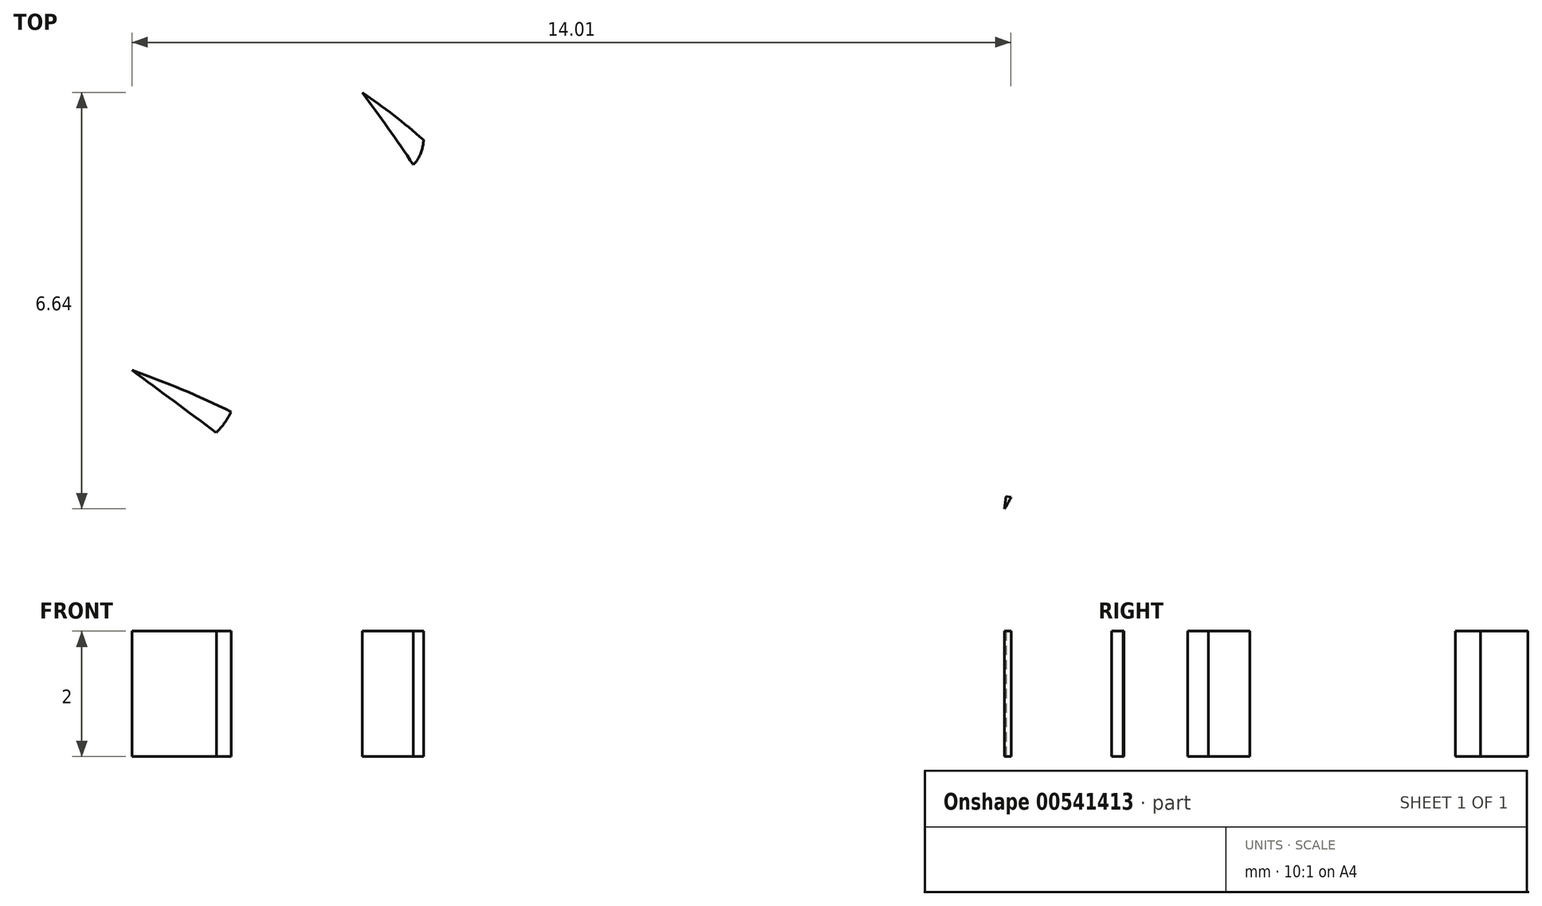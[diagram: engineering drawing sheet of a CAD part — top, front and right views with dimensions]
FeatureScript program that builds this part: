
annotation { "Feature Type Name" : "Feature", "Feature Type Description" : "" }
export const myFeature = defineFeature(function(context is Context, id is Id, definition is map)
    precondition{}
    {
        {
            var Q0;
            Q0=qCreatedBy(makeId("Top.planeOp"),FACE);
            var sketch = newSketch(context, id + "F0", { "sketchPlane" : qUnion([Q0])});
            skFitSpline(sketch, "E0", {"points": [v(-7.28, 23.86) * mm, v(-2.86, 13.8) * mm, v(-10.95, 19.43) * mm], "startDerivative": vector(18.39, -24.25) * mm, "endDerivative": vector(-31.57, 11.1) * mm});
            skFitSpline(sketch, "E1", {"points": [v(-7.28, 23.86) * mm, v(-3.4, 19.4) * mm, v(-2.4, 24.55) * mm], "startDerivative": vector(15.72, -10.48) * mm, "endDerivative": vector(5.56, 16.47) * mm});
            skFitSpline(sketch, "E2", {"points": [v(-2.4, 24.55) * mm, v(-1.89, 15.31) * mm, v(-0.1, 9.05) * mm], "startDerivative": vector(-4.2, -34.55) * mm, "endDerivative": vector(9.1, -27.73) * mm});
            skFitSpline(sketch, "E3", {"points": [v(2.74, 21.8) * mm, v(2.33, 14.08) * mm, v(-0.1, 9.05) * mm], "startDerivative": vector(3.5, -17.09) * mm, "endDerivative": vector(-8.14, -6.33) * mm});
            skFitSpline(sketch, "E4", {"points": [v(2.74, 21.8) * mm, v(3.37, 15.56) * mm, v(2.5, 12.07) * mm], "startDerivative": vector(6.44, -9.2) * mm, "endDerivative": vector(-5.09, -24.27) * mm});
            skFitSpline(sketch, "E5", {"points": [v(2.5, 12.07) * mm, v(5.64, 13.91) * mm, v(9.18, 17.17) * mm], "startDerivative": vector(11.84, 4.8) * mm, "endDerivative": vector(6.3, 8.36) * mm});
            skFitSpline(sketch, "E6", {"points": [v(9.18, 17.17) * mm, v(6.35, 13.6) * mm, v(2.5, 10.84) * mm], "startDerivative": vector(-3.85, -9.64) * mm, "endDerivative": vector(-10.17, -6.25) * mm});
            skFitSpline(sketch, "E7", {"points": [v(-2, 11.23) * mm, v(-1.24, 6.46) * mm, v(-1.28, 2.27) * mm], "startDerivative": vector(2.67, -9.53) * mm, "endDerivative": vector(-2.9, -13.25) * mm});
            skFitSpline(sketch, "E8", {"points": [v(2.5, 10.84) * mm, v(0.47, 6.67) * mm, v(1.91, -4.86) * mm], "startDerivative": vector(-6.92, -10.08) * mm, "endDerivative": vector(0, 3.84) * mm});
            skFitSpline(sketch, "E9", {"points": [v(-10.1, 11.97) * mm, v(-6.04, 6.59) * mm, v(-1.28, 2.27) * mm], "startDerivative": vector(-0.34, -15.68) * mm, "endDerivative": vector(0, 6.82) * mm});
            skFitSpline(sketch, "E10", {"points": [v(10.4, 11.36) * mm, v(7.8, 1.76) * mm, v(1.91, -4.86) * mm], "startDerivative": vector(-2.43, -20.8) * mm, "endDerivative": vector(-4.14, 2.7) * mm});
            skFitSpline(sketch, "E11", {"points": [v(10.4, 11.36) * mm, v(9.84, 4.76) * mm, v(7.52, -0.1) * mm], "startDerivative": vector(5.3, -7.8) * mm, "endDerivative": vector(-5.92, -9.7) * mm});
            skFitSpline(sketch, "E12", {"points": [v(7.52, -0.1) * mm, v(13.28, 2.8) * mm, v(21.16, 4.47) * mm], "startDerivative": vector(11.55, 6.87) * mm, "endDerivative": vector(21.33, -3.14) * mm});
            skFitSpline(sketch, "E13", {"points": [v(-10.1, 11.97) * mm, v(-9.26, 8.16) * mm, v(-16.19, 10.72) * mm], "startDerivative": vector(-8.08, -15.34) * mm, "endDerivative": vector(-18.86, 4.84) * mm});
            skFitSpline(sketch, "E14", {"points": [v(-16.19, 10.72) * mm, v(-6.94, 6.04) * mm, v(-16.19, 5.22) * mm], "startDerivative": vector(40.48, -21.8) * mm, "endDerivative": vector(-62.27, 1.8) * mm});
            skFitSpline(sketch, "E15", {"points": [v(-1.35, -0.04) * mm, v(-1.42, -8.86) * mm, v(-20.96, 0.93) * mm], "startDerivative": vector(7.31, -30.06) * mm, "endDerivative": vector(-51.62, -16.27) * mm});
            skFitSpline(sketch, "E16", {"points": [v(11.85, 1.07) * mm, v(2.54, -18.35) * mm, v(5.68, -37.82) * mm], "startDerivative": vector(-64.96, -24.6) * mm, "endDerivative": vector(16.53, -39.43) * mm});
            skFitSpline(sketch, "E17", {"points": [v(11.85, 1.07) * mm, v(19.18, 1.07) * mm, v(12.97, 1.76) * mm], "startDerivative": vector(22.33, -1.93) * mm, "endDerivative": vector(-7.46, -0.54) * mm});
            skFitSpline(sketch, "E18", {"points": [v(12.97, 1.76) * mm, v(16.44, 3.4) * mm, v(21.16, 4.47) * mm], "startDerivative": vector(7, 3.83) * mm, "endDerivative": vector(9.33, 1.62) * mm});
            skFitSpline(sketch, "E19", {"points": [v(-20.96, 0.93) * mm, v(-6.66, -5.68) * mm, v(-18.96, -5.83) * mm], "startDerivative": vector(45.61, 4.03) * mm, "endDerivative": vector(-48.6, -15.15) * mm});
            skFitSpline(sketch, "E20", {"points": [v(-18.96, -5.83) * mm, v(-1.16, -18.25) * mm, v(-8.26, -37.47) * mm], "startDerivative": vector(95.98, 3.77) * mm, "endDerivative": vector(-30.97, -39) * mm});
            skLineSegment(sketch, "E21", {"start": v(-8.26, -37.47) * mm, "end": v(5.68, -37.82) * mm});
            skFitSpline(sketch, "E22", {"points": [v(-13.45, 22.99) * mm, v(-14.02, 22.6) * mm, v(-13.4, 21.65) * mm], "startDerivative": vector(1.91, -4.42) * mm, "endDerivative": vector(-3.84, -0.79) * mm});
            skFitSpline(sketch, "E23", {"points": [v(-13.4, 21.65) * mm, v(-12.9, 20.9) * mm, v(-12.95, 20.25) * mm], "startDerivative": vector(-4.2, -3.2) * mm, "endDerivative": vector(-4.26, -2.28) * mm});
            skFitSpline(sketch, "E24", {"points": [v(-12.95, 20.25) * mm, v(-11.98, 19.71) * mm, v(-11.6, 19.12) * mm], "startDerivative": vector(-2.53, -3.4) * mm, "endDerivative": vector(-2.97, -4.02) * mm});
            skFitSpline(sketch, "E25", {"points": [v(-11.6, 19.12) * mm, v(-10.75, 18.89) * mm, v(-10.27, 18.52) * mm], "startDerivative": vector(-0.2, -3.23) * mm, "endDerivative": vector(1.3, -3.45) * mm});
            skFitSpline(sketch, "E26", {"points": [v(-10.27, 18.52) * mm, v(-9.31, 18.95) * mm, v(-9.34, 19.63) * mm], "startDerivative": vector(1.56, -3.6) * mm, "endDerivative": vector(1.97, 2.6) * mm});
            skFitSpline(sketch, "E27", {"points": [v(-9.34, 19.63) * mm, v(-9.7, 19.93) * mm, v(-9.46, 20.67) * mm], "startDerivative": vector(1.95, 4.8) * mm, "endDerivative": vector(2.77, 2.16) * mm});
            skFitSpline(sketch, "E28", {"points": [v(-9.46, 20.67) * mm, v(-9.73, 21.28) * mm, v(-10.33, 22.47) * mm], "startDerivative": vector(1.33, 6.6) * mm, "endDerivative": vector(1.65, 8.03) * mm});
            skFitSpline(sketch, "E29", {"points": [v(-10.33, 22.47) * mm, v(-10.9, 22.62) * mm, v(-11.47, 23.44) * mm], "startDerivative": vector(-1.13, 5.1) * mm, "endDerivative": vector(-0.22, 4.49) * mm});
            skFitSpline(sketch, "E30", {"points": [v(-11.47, 23.44) * mm, v(-12.2, 23.5) * mm, v(-12.48, 23.71) * mm], "startDerivative": vector(-1.3, 4.81) * mm, "endDerivative": vector(-1.53, 3.53) * mm});
            skFitSpline(sketch, "E31", {"points": [v(-12.48, 23.71) * mm, v(-13.17, 23.6) * mm, v(-13.45, 22.99) * mm], "startDerivative": vector(-1.7, -4.44) * mm, "endDerivative": vector(2.22, -3.82) * mm});
            skFitSpline(sketch, "E32", {"points": [v(-1.35, 21.75) * mm, v(-1.42, 21.15) * mm, v(-1.8, 20.76) * mm], "startDerivative": vector(-0.58, -0.6) * mm, "endDerivative": vector(1.68, -4.51) * mm});
            skFitSpline(sketch, "E33", {"points": [v(-1.8, 20.76) * mm, v(-2.11, 20.22) * mm, v(-1.78, 19.23) * mm], "startDerivative": vector(2.85, -4.12) * mm, "endDerivative": vector(3.48, -0.95) * mm});
            skFitSpline(sketch, "E34", {"points": [v(-1.78, 19.23) * mm, v(-1.62, 18.4) * mm, v(-1.1, 17.14) * mm], "startDerivative": vector(5.03, -3.08) * mm, "endDerivative": vector(9.15, -4.78) * mm});
            skFitSpline(sketch, "E35", {"points": [v(-1.1, 17.14) * mm, v(-0.27, 16.66) * mm, v(0.64, 15.82) * mm], "startDerivative": vector(7.65, 0.86) * mm, "endDerivative": vector(9.97, 1.24) * mm});
            skFitSpline(sketch, "E36", {"points": [v(0.64, 15.82) * mm, v(1.16, 15.52) * mm, v(2.74, 14.9) * mm], "startDerivative": vector(7.16, 2.4) * mm, "endDerivative": vector(7.15, 0.46) * mm});
            skFitSpline(sketch, "E37", {"points": [v(2.74, 14.9) * mm, v(2.92, 15.97) * mm, v(3.06, 17.4) * mm], "startDerivative": vector(3.53, 0.84) * mm, "endDerivative": vector(3.33, 5.77) * mm});
            skFitSpline(sketch, "E38", {"points": [v(3.06, 17.4) * mm, v(2.13, 17.82) * mm, v(2.59, 19.14) * mm], "startDerivative": vector(-4.3, 0.6) * mm, "endDerivative": vector(0.65, 3.2) * mm});
            skFitSpline(sketch, "E39", {"points": [v(2.59, 19.14) * mm, v(2, 19.76) * mm, v(1.42, 21.07) * mm], "startDerivative": vector(1.7, 10.1) * mm, "endDerivative": vector(0.5, 6.87) * mm});
            skFitSpline(sketch, "E40", {"points": [v(1.42, 21.07) * mm, v(0.65, 21) * mm, v(0.13, 21.39) * mm], "startDerivative": vector(-1.39, 4.09) * mm, "endDerivative": vector(-0.65, 3.22) * mm});
            skFitSpline(sketch, "E41", {"points": [v(0.13, 21.39) * mm, v(-0.36, 21.67) * mm, v(-1.35, 21.75) * mm], "startDerivative": vector(0.09, 6.17) * mm, "endDerivative": vector(1.27, -4.42) * mm});
            skFitSpline(sketch, "E42", {"points": [v(-7.74, 24.94) * mm, v(-7.9, 24.36) * mm, v(-7.99, 24.08) * mm], "startDerivative": vector(-3.6, -2.32) * mm, "endDerivative": vector(-2.86, -0.7) * mm});
            skFitSpline(sketch, "E43", {"points": [v(-7.74, 24.94) * mm, v(-7.15, 25.05) * mm, v(-6.77, 24.94) * mm], "startDerivative": vector(0.18, 4.05) * mm, "endDerivative": vector(2.06, 1.76) * mm});
            skFitSpline(sketch, "E44", {"points": [v(-7.99, 24.08) * mm, v(-7.72, 23.7) * mm, v(-7.67, 23.34) * mm], "startDerivative": vector(-2.5, -1.08) * mm, "endDerivative": vector(-1.66, -1.55) * mm});
            skFitSpline(sketch, "E45", {"points": [v(-7.67, 23.34) * mm, v(-7.26, 23.1) * mm, v(-6.94, 22.85) * mm], "startDerivative": vector(-1.07, -1.26) * mm, "endDerivative": vector(0.16, -2.2) * mm});
            skFitSpline(sketch, "E46", {"points": [v(-6.77, 24.94) * mm, v(-6.7, 24.49) * mm, v(-6.33, 24.46) * mm], "startDerivative": vector(3.01, 1.48) * mm, "endDerivative": vector(0.95, 0.14) * mm});
            skFitSpline(sketch, "E47", {"points": [v(-6.33, 24.46) * mm, v(-6.38, 24.01) * mm, v(-6.36, 23.7) * mm], "startDerivative": vector(2.09, 0.16) * mm, "endDerivative": vector(3.63, -0.22) * mm});
            skFitSpline(sketch, "E48", {"points": [v(-6.36, 23.7) * mm, v(-6.35, 23.3) * mm, v(-6.94, 22.85) * mm], "startDerivative": vector(-3.48, -2.93) * mm, "endDerivative": vector(-2.38, 3.1) * mm});
            skFitSpline(sketch, "E49", {"points": [v(-1.77, 29.16) * mm, v(-2.43, 29.34) * mm, v(-2.76, 28.26) * mm], "startDerivative": vector(-2.15, -4.3) * mm, "endDerivative": vector(-3.07, 2.43) * mm});
            skFitSpline(sketch, "E50", {"points": [v(-2.76, 28.26) * mm, v(-3.01, 27.4) * mm, v(-3.54, 27.02) * mm], "startDerivative": vector(-5.15, 1.16) * mm, "endDerivative": vector(-4.49, 1.8) * mm});
            skFitSpline(sketch, "E51", {"points": [v(-3.54, 27.02) * mm, v(-3.33, 25.93) * mm, v(-3.54, 25.26) * mm], "startDerivative": vector(-4.22, -0.25) * mm, "endDerivative": vector(-5, -0.31) * mm});
            skFitSpline(sketch, "E52", {"points": [v(-3.54, 25.26) * mm, v(-3.17, 24.46) * mm, v(-3.17, 23.94) * mm], "startDerivative": vector(-2.6, -1.92) * mm, "endDerivative": vector(-1.81, -3.2) * mm});
            skFitSpline(sketch, "E53", {"points": [v(-3.17, 23.94) * mm, v(-2.2, 23.4) * mm, v(-1.72, 23.94) * mm], "startDerivative": vector(-1.75, -3.5) * mm, "endDerivative": vector(3.25, 0.15) * mm});
            skFitSpline(sketch, "E54", {"points": [v(-1.72, 23.94) * mm, v(-1.72, 24.4) * mm, v(-0.98, 24.62) * mm], "startDerivative": vector(4.92, 1.59) * mm, "endDerivative": vector(3.43, -0.74) * mm});
            skFitSpline(sketch, "E55", {"points": [v(-0.98, 24.62) * mm, v(-0.68, 25.22) * mm, v(-0.15, 26.44) * mm], "startDerivative": vector(5.92, 3.23) * mm, "endDerivative": vector(7.21, 3.9) * mm});
            skFitSpline(sketch, "E56", {"points": [v(-0.15, 26.44) * mm, v(-0.4, 26.97) * mm, v(-0.15, 27.94) * mm], "startDerivative": vector(3.19, 4.14) * mm, "endDerivative": vector(3.3, 3.05) * mm});
            skFitSpline(sketch, "E57", {"points": [v(-0.15, 27.94) * mm, v(-0.57, 28.53) * mm, v(-0.6, 28.88) * mm], "startDerivative": vector(2.85, 4.1) * mm, "endDerivative": vector(1.72, 3.44) * mm});
            skFitSpline(sketch, "E58", {"points": [v(-0.6, 28.88) * mm, v(-1.12, 29.34) * mm, v(-1.77, 29.16) * mm], "startDerivative": vector(-4.49, -1.55) * mm, "endDerivative": vector(-1.5, -4.15) * mm});
            skFitSpline(sketch, "E59", {"points": [v(-9.51, 16.2) * mm, v(-10.18, 16.4) * mm, v(-10.5, 15.3) * mm], "startDerivative": vector(-2.15, -4.3) * mm, "endDerivative": vector(-3.07, 2.43) * mm});
            skFitSpline(sketch, "E60", {"points": [v(-10.5, 15.3) * mm, v(-10.76, 14.46) * mm, v(-11.29, 14.06) * mm], "startDerivative": vector(-5.15, 1.16) * mm, "endDerivative": vector(-4.49, 1.8) * mm});
            skFitSpline(sketch, "E61", {"points": [v(-11.29, 14.06) * mm, v(-11.08, 12.98) * mm, v(-11.29, 12.31) * mm], "startDerivative": vector(-4.22, -0.25) * mm, "endDerivative": vector(-5, -0.31) * mm});
            skFitSpline(sketch, "E62", {"points": [v(-11.29, 12.31) * mm, v(-10.92, 11.5) * mm, v(-10.9, 10.9) * mm], "startDerivative": vector(-2.6, -1.92) * mm, "endDerivative": vector(-1.81, -3.2) * mm});
            skFitSpline(sketch, "E63", {"points": [v(-10.9, 10.9) * mm, v(-9.95, 10.45) * mm, v(-9.44, 10.9) * mm], "startDerivative": vector(-1.75, -3.5) * mm, "endDerivative": vector(3.25, 0.15) * mm});
            skFitSpline(sketch, "E64", {"points": [v(-9.44, 10.9) * mm, v(-9.44, 11.37) * mm, v(-8.73, 11.67) * mm], "startDerivative": vector(4.92, 1.59) * mm, "endDerivative": vector(3.43, -0.74) * mm});
            skFitSpline(sketch, "E65", {"points": [v(-8.73, 11.67) * mm, v(-8.43, 12.27) * mm, v(-7.9, 13.49) * mm], "startDerivative": vector(5.92, 3.23) * mm, "endDerivative": vector(7.21, 3.9) * mm});
            skFitSpline(sketch, "E66", {"points": [v(-7.9, 13.49) * mm, v(-8.15, 14.02) * mm, v(-7.9, 14.99) * mm], "startDerivative": vector(3.19, 4.14) * mm, "endDerivative": vector(3.3, 3.05) * mm});
            skFitSpline(sketch, "E67", {"points": [v(-7.9, 14.99) * mm, v(-8.31, 15.58) * mm, v(-8.34, 15.93) * mm], "startDerivative": vector(2.85, 4.1) * mm, "endDerivative": vector(1.72, 3.44) * mm});
            skFitSpline(sketch, "E68", {"points": [v(-8.34, 15.93) * mm, v(-8.87, 16.4) * mm, v(-9.51, 16.2) * mm], "startDerivative": vector(-4.49, -1.55) * mm, "endDerivative": vector(-1.5, -4.15) * mm});
            skFitSpline(sketch, "E69", {"points": [v(20.11, 9.78) * mm, v(19.52, 10.13) * mm, v(18.92, 9.17) * mm], "startDerivative": vector(-3.2, -3.6) * mm, "endDerivative": vector(-2.34, 3.14) * mm});
            skFitSpline(sketch, "E70", {"points": [v(18.92, 9.17) * mm, v(18.46, 8.41) * mm, v(17.84, 8.17) * mm], "startDerivative": vector(-4.67, 2.45) * mm, "endDerivative": vector(-3.87, 2.9) * mm});
            skFitSpline(sketch, "E71", {"points": [v(17.84, 8.17) * mm, v(17.76, 7.07) * mm, v(17.4, 6.48) * mm], "startDerivative": vector(-4.14, 0.85) * mm, "endDerivative": vector(-4.9, 1) * mm});
            skFitSpline(sketch, "E72", {"points": [v(17.4, 6.48) * mm, v(17.54, 5.6) * mm, v(17.4, 5.02) * mm], "startDerivative": vector(-3.01, -1.18) * mm, "endDerivative": vector(-2.58, -2.63) * mm});
            skFitSpline(sketch, "E73", {"points": [v(17.4, 5.02) * mm, v(18.2, 4.33) * mm, v(18.8, 4.64) * mm], "startDerivative": vector(-2.6, -2.93) * mm, "endDerivative": vector(3.18, -0.7) * mm});
            skFitSpline(sketch, "E74", {"points": [v(18.8, 4.64) * mm, v(18.93, 5.09) * mm, v(19.7, 5.2) * mm], "startDerivative": vector(5.17, 0.26) * mm, "endDerivative": vector(3.12, -1.6) * mm});
            skFitSpline(sketch, "E75", {"points": [v(19.7, 5.2) * mm, v(20.14, 5.7) * mm, v(20.97, 6.74) * mm], "startDerivative": vector(6.55, 1.59) * mm, "endDerivative": vector(7.98, 1.9) * mm});
            skFitSpline(sketch, "E76", {"points": [v(20.97, 6.74) * mm, v(20.86, 7.32) * mm, v(21.36, 8.18) * mm], "startDerivative": vector(4.15, 3.18) * mm, "endDerivative": vector(3.98, 2.1) * mm});
            skFitSpline(sketch, "E77", {"points": [v(21.36, 8.18) * mm, v(21.1, 8.86) * mm, v(21.18, 9.21) * mm], "startDerivative": vector(3.81, 3.21) * mm, "endDerivative": vector(2.55, 2.88) * mm});
            skFitSpline(sketch, "E78", {"points": [v(21.18, 9.21) * mm, v(20.79, 9.8) * mm, v(20.11, 9.78) * mm], "startDerivative": vector(-4.74, -0.34) * mm, "endDerivative": vector(-2.52, -3.62) * mm});
            skFitSpline(sketch, "E79", {"points": [v(5.29, 16.4) * mm, v(5.13, 15.83) * mm, v(5.04, 15.54) * mm], "startDerivative": vector(-3.6, -2.32) * mm, "endDerivative": vector(-2.86, -0.7) * mm});
            skFitSpline(sketch, "E80", {"points": [v(5.29, 16.4) * mm, v(5.88, 16.52) * mm, v(6.25, 16.4) * mm], "startDerivative": vector(0.18, 4.05) * mm, "endDerivative": vector(2.06, 1.76) * mm});
            skFitSpline(sketch, "E81", {"points": [v(5.04, 15.54) * mm, v(5.3, 15.16) * mm, v(5.36, 14.8) * mm], "startDerivative": vector(-2.5, -1.08) * mm, "endDerivative": vector(-1.66, -1.55) * mm});
            skFitSpline(sketch, "E82", {"points": [v(5.36, 14.8) * mm, v(5.76, 14.56) * mm, v(6.09, 14.32) * mm], "startDerivative": vector(-1.07, -1.26) * mm, "endDerivative": vector(0.16, -2.2) * mm});
            skFitSpline(sketch, "E83", {"points": [v(6.25, 16.4) * mm, v(6.32, 15.95) * mm, v(6.7, 15.93) * mm], "startDerivative": vector(3.01, 1.48) * mm, "endDerivative": vector(0.95, 0.14) * mm});
            skFitSpline(sketch, "E84", {"points": [v(6.7, 15.93) * mm, v(6.65, 15.48) * mm, v(6.67, 15.16) * mm], "startDerivative": vector(2.09, 0.16) * mm, "endDerivative": vector(3.63, -0.22) * mm});
            skFitSpline(sketch, "E85", {"points": [v(6.67, 15.16) * mm, v(6.68, 14.76) * mm, v(6.09, 14.32) * mm], "startDerivative": vector(-3.48, -2.93) * mm, "endDerivative": vector(-2.38, 3.1) * mm});
            skFitSpline(sketch, "E86", {"points": [v(6.3, 11.03) * mm, v(6.2, 11.62) * mm, v(6.15, 11.91) * mm], "startDerivative": vector(2.28, 3.62) * mm, "endDerivative": vector(2.3, 1.83) * mm});
            skFitSpline(sketch, "E87", {"points": [v(6.3, 11.03) * mm, v(5.8, 10.67) * mm, v(5.42, 10.62) * mm], "startDerivative": vector(1.55, -3.75) * mm, "endDerivative": vector(-1.12, -2.47) * mm});
            skFitSpline(sketch, "E88", {"points": [v(6.15, 11.91) * mm, v(5.75, 12.14) * mm, v(5.56, 12.44) * mm], "startDerivative": vector(1.8, 2.03) * mm, "endDerivative": vector(0.85, 2.1) * mm});
            skFitSpline(sketch, "E89", {"points": [v(5.56, 12.44) * mm, v(5.08, 12.5) * mm, v(4.69, 12.58) * mm], "startDerivative": vector(0.43, 1.6) * mm, "endDerivative": vector(-1.07, 1.92) * mm});
            skFitSpline(sketch, "E90", {"points": [v(5.42, 10.62) * mm, v(5.17, 11) * mm, v(4.82, 10.87) * mm], "startDerivative": vector(-2.1, -2.61) * mm, "endDerivative": vector(-0.8, -0.53) * mm});
            skFitSpline(sketch, "E91", {"points": [v(4.82, 10.87) * mm, v(4.67, 11.3) * mm, v(4.52, 11.57) * mm], "startDerivative": vector(-1.82, -1.03) * mm, "endDerivative": vector(-3.38, -1.34) * mm});
            skFitSpline(sketch, "E92", {"points": [v(4.52, 11.57) * mm, v(4.34, 11.93) * mm, v(4.69, 12.58) * mm], "startDerivative": vector(1.92, 4.13) * mm, "endDerivative": vector(3.47, -1.8) * mm});
            skFitSpline(sketch, "E93", {"points": [v(6.28, 4.1) * mm, v(6.36, 3.5) * mm, v(6.39, 3.21) * mm], "startDerivative": vector(-2.42, -3.53) * mm, "endDerivative": vector(-2.36, -1.74) * mm});
            skFitSpline(sketch, "E94", {"points": [v(6.28, 4.1) * mm, v(6.78, 3.63) * mm, v(7.17, 3.66) * mm], "startDerivative": vector(-1.4, 3.8) * mm, "endDerivative": vector(1.21, 2.42) * mm});
            skFitSpline(sketch, "E95", {"points": [v(6.39, 3.21) * mm, v(6.78, 2.15) * mm, v(6.96, 1.85) * mm], "startDerivative": vector(-1.89, -1.96) * mm, "endDerivative": vector(-0.93, -2.07) * mm});
            skFitSpline(sketch, "E96", {"points": [v(6.96, 1.85) * mm, v(7.44, 1.77) * mm, v(7.9, 1.66) * mm], "startDerivative": vector(-0.5, -1.58) * mm, "endDerivative": vector(1, -1.95) * mm});
            skFitSpline(sketch, "E97", {"points": [v(7.17, 3.66) * mm, v(7.4, 3.27) * mm, v(7.77, 3.4) * mm], "startDerivative": vector(2.2, 2.53) * mm, "endDerivative": vector(0.82, 0.5) * mm});
            skFitSpline(sketch, "E98", {"points": [v(7.77, 3.4) * mm, v(7.9, 2.96) * mm, v(8.04, 2.68) * mm], "startDerivative": vector(1.86, 0.96) * mm, "endDerivative": vector(3.43, 1.2) * mm});
            skFitSpline(sketch, "E99", {"points": [v(8.04, 2.68) * mm, v(8.2, 2.3) * mm, v(7.9, 1.66) * mm], "startDerivative": vector(-2.08, -4.05) * mm, "endDerivative": vector(-3.4, 1.94) * mm});
            skFitSpline(sketch, "E100.trimOffspring", {"points": [v(10.4, 11.36) * mm, v(7.8, 1.76) * mm, v(1.91, -4.86) * mm], "startDerivative": vector(-2.43, -20.8) * mm, "endDerivative": vector(-4.14, 2.7) * mm});
            skFitSpline(sketch, "E101.trimOffspring", {"points": [v(-10.95, 19.43) * mm, v(-6.18, 15.66) * mm, v(-2, 11.23) * mm], "startDerivative": vector(26.16, -19.3) * mm, "endDerivative": vector(2.9, -7.26) * mm});
            skFitSpline(sketch, "E102", {"points": [v(-4.73, 1.23) * mm, v(-5.27, 1.66) * mm, v(-6, 0.78) * mm], "startDerivative": vector(-3.65, -3.14) * mm, "endDerivative": vector(-1.9, 3.43) * mm});
            skFitSpline(sketch, "E103", {"points": [v(-6, 0.78) * mm, v(-6.55, 0.1) * mm, v(-7.2, -0.06) * mm], "startDerivative": vector(-4.3, 3.05) * mm, "endDerivative": vector(-3.45, 3.39) * mm});
            skFitSpline(sketch, "E104", {"points": [v(-7.2, -0.06) * mm, v(-7.42, -1.14) * mm, v(-7.87, -1.68) * mm], "startDerivative": vector(-4, 1.4) * mm, "endDerivative": vector(-4.73, 1.64) * mm});
            skFitSpline(sketch, "E105", {"points": [v(-7.87, -1.68) * mm, v(-7.84, -2.56) * mm, v(-8.05, -3.13) * mm], "startDerivative": vector(-3.15, -0.77) * mm, "endDerivative": vector(-2.91, -2.26) * mm});
            skFitSpline(sketch, "E106", {"points": [v(-6.71, -3.69) * mm, v(-6.53, -3.26) * mm, v(-5.76, -3.26) * mm], "startDerivative": vector(5.16, -0.43) * mm, "endDerivative": vector(2.88, -2) * mm});
            skFitSpline(sketch, "E107", {"points": [v(-5.76, -3.26) * mm, v(-5.25, -2.82) * mm, v(-4.3, -1.9) * mm], "startDerivative": vector(6.7, 0.7) * mm, "endDerivative": vector(8.16, 0.82) * mm});
            skFitSpline(sketch, "E108", {"points": [v(-4.3, -1.9) * mm, v(-4.32, -1.31) * mm, v(-3.71, -0.52) * mm], "startDerivative": vector(4.54, 2.6) * mm, "endDerivative": vector(4.22, 1.54) * mm});
            skFitSpline(sketch, "E109", {"points": [v(-3.71, -0.52) * mm, v(-3.87, 0.19) * mm, v(-3.75, 0.52) * mm], "startDerivative": vector(4.2, 2.67) * mm, "endDerivative": vector(2.92, 2.51) * mm});
            skFitSpline(sketch, "E110", {"points": [v(-3.75, 0.52) * mm, v(-4.06, 1.15) * mm, v(-4.73, 1.23) * mm], "startDerivative": vector(-4.74, 0.3) * mm, "endDerivative": vector(-2.99, -3.25) * mm});
            skFitSpline(sketch, "E111.trimOffspring", {"points": [v(-8.05, -3.13) * mm, v(-6.71, -3.69) * mm], "startDerivative": vector(-2.96, -2.55) * mm, "endDerivative": vector(3.06, -1.11) * mm});
            skFitSpline(sketch, "E112", {"points": [v(-15.86, 12.52) * mm, v(-16.13, 12) * mm, v(-16.28, 11.74) * mm], "startDerivative": vector(-4, -1.5) * mm, "endDerivative": vector(-2.94, -0.07) * mm});
            skFitSpline(sketch, "E113", {"points": [v(-15.86, 12.52) * mm, v(-15.25, 12.51) * mm, v(-14.91, 12.32) * mm], "startDerivative": vector(1.03, 3.92) * mm, "endDerivative": vector(2.38, 1.29) * mm});
            skFitSpline(sketch, "E114", {"points": [v(-16.28, 11.74) * mm, v(-16.1, 11.3) * mm, v(-16.12, 10.95) * mm], "startDerivative": vector(-2.67, -0.52) * mm, "endDerivative": vector(-1.95, -1.16) * mm});
            skFitSpline(sketch, "E115", {"points": [v(-16.12, 10.95) * mm, v(-15.78, 10.62) * mm, v(-15.51, 10.36) * mm], "startDerivative": vector(-1.3, -1) * mm, "endDerivative": vector(-0.3, -2.18) * mm});
            skFitSpline(sketch, "E116", {"points": [v(-14.91, 12.32) * mm, v(-14.94, 11.86) * mm, v(-14.58, 11.76) * mm], "startDerivative": vector(3.26, 0.8) * mm, "endDerivative": vector(0.95, -0.06) * mm});
            skFitSpline(sketch, "E117", {"points": [v(-14.58, 11.76) * mm, v(-14.72, 11.33) * mm, v(-14.77, 10.96) * mm], "startDerivative": vector(2.08, -0.28) * mm, "endDerivative": vector(3.5, -0.98) * mm});
            skFitSpline(sketch, "E118", {"points": [v(-14.77, 10.96) * mm, v(-14.9, 10.35) * mm, v(-15.52, 10.36) * mm], "startDerivative": vector(5.36, 1.26) * mm, "endDerivative": vector(-0.5, 1.78) * mm});
            skFitSpline(sketch, "E119", {"points": [v(7.87, 7.48) * mm, v(7.95, 6.89) * mm, v(7.98, 6.59) * mm], "startDerivative": vector(-2.42, -3.53) * mm, "endDerivative": vector(-2.36, -1.74) * mm});
            skFitSpline(sketch, "E120", {"points": [v(7.87, 7.48) * mm, v(8.38, 7.81) * mm, v(8.76, 7.85) * mm], "startDerivative": vector(-1.4, 3.8) * mm, "endDerivative": vector(1.21, 2.42) * mm});
            skFitSpline(sketch, "E121", {"points": [v(7.98, 6.59) * mm, v(8.37, 6.34) * mm, v(8.55, 6.03) * mm], "startDerivative": vector(-1.89, -1.96) * mm, "endDerivative": vector(-0.93, -2.07) * mm});
            skFitSpline(sketch, "E122", {"points": [v(8.55, 6.03) * mm, v(9.03, 5.96) * mm, v(9.51, 5.84) * mm], "startDerivative": vector(-0.5, -1.58) * mm, "endDerivative": vector(1, -1.96) * mm});
            skFitSpline(sketch, "E123", {"points": [v(8.76, 7.85) * mm, v(9, 7.46) * mm, v(9.36, 7.58) * mm], "startDerivative": vector(2.2, 2.53) * mm, "endDerivative": vector(0.82, 0.5) * mm});
            skFitSpline(sketch, "E124", {"points": [v(9.36, 7.58) * mm, v(9.49, 7.15) * mm, v(9.54, 6.94) * mm], "startDerivative": vector(0.76, 2.2) * mm, "endDerivative": vector(3.08, -0.25) * mm});
            skFitSpline(sketch, "E125", {"points": [v(9.54, 6.94) * mm, v(9.78, 6.5) * mm, v(9.51, 5.84) * mm], "startDerivative": vector(-2.3, -2.17) * mm, "endDerivative": vector(-3.4, 1.94) * mm});
            skFitSpline(sketch, "E126", {"points": [v(9.64, 22.25) * mm, v(8.97, 22.43) * mm, v(8.65, 21.35) * mm], "startDerivative": vector(-2.15, -4.3) * mm, "endDerivative": vector(-3.07, 2.43) * mm});
            skFitSpline(sketch, "E127", {"points": [v(8.65, 21.35) * mm, v(8.4, 20.5) * mm, v(7.87, 20.1) * mm], "startDerivative": vector(-5.15, 1.16) * mm, "endDerivative": vector(-4.49, 1.8) * mm});
            skFitSpline(sketch, "E128", {"points": [v(7.87, 20.1) * mm, v(8.07, 19.02) * mm, v(7.87, 18.35) * mm], "startDerivative": vector(-4.22, -0.25) * mm, "endDerivative": vector(-5, -0.31) * mm});
            skFitSpline(sketch, "E129", {"points": [v(7.87, 18.35) * mm, v(8.24, 17.54) * mm, v(8.26, 16.94) * mm], "startDerivative": vector(-2.6, -1.92) * mm, "endDerivative": vector(-1.81, -3.2) * mm});
            skFitSpline(sketch, "E130", {"points": [v(8.26, 16.94) * mm, v(9.2, 16.48) * mm, v(9.71, 16.94) * mm], "startDerivative": vector(-1.75, -3.5) * mm, "endDerivative": vector(3.25, 0.15) * mm});
            skFitSpline(sketch, "E131", {"points": [v(9.71, 16.94) * mm, v(9.71, 17.4) * mm, v(10.43, 17.7) * mm], "startDerivative": vector(4.92, 1.59) * mm, "endDerivative": vector(3.43, -0.74) * mm});
            skFitSpline(sketch, "E132", {"points": [v(10.43, 17.7) * mm, v(10.73, 18.3) * mm, v(11.26, 19.53) * mm], "startDerivative": vector(5.92, 3.23) * mm, "endDerivative": vector(7.21, 3.9) * mm});
            skFitSpline(sketch, "E133", {"points": [v(11.26, 19.53) * mm, v(11, 20.06) * mm, v(11.26, 21.02) * mm], "startDerivative": vector(3.19, 4.14) * mm, "endDerivative": vector(3.3, 3.05) * mm});
            skFitSpline(sketch, "E134", {"points": [v(11.26, 21.02) * mm, v(10.84, 21.62) * mm, v(10.82, 21.97) * mm], "startDerivative": vector(2.85, 4.1) * mm, "endDerivative": vector(1.72, 3.44) * mm});
            skFitSpline(sketch, "E135", {"points": [v(10.82, 21.97) * mm, v(10.29, 22.43) * mm, v(9.64, 22.25) * mm], "startDerivative": vector(-4.49, -1.55) * mm, "endDerivative": vector(-1.5, -4.15) * mm});
            skFitSpline(sketch, "E136", {"points": [v(11.28, 16.25) * mm, v(10.61, 16.43) * mm, v(10.3, 15.35) * mm], "startDerivative": vector(-2.15, -4.3) * mm, "endDerivative": vector(-3.07, 2.43) * mm});
            skFitSpline(sketch, "E137", {"points": [v(10.3, 15.35) * mm, v(10.04, 14.5) * mm, v(9.5, 14.1) * mm], "startDerivative": vector(-5.15, 1.16) * mm, "endDerivative": vector(-4.49, 1.8) * mm});
            skFitSpline(sketch, "E138", {"points": [v(9.5, 14.1) * mm, v(9.72, 13.02) * mm, v(9.5, 12.35) * mm], "startDerivative": vector(-4.22, -0.25) * mm, "endDerivative": vector(-5, -0.31) * mm});
            skFitSpline(sketch, "E139", {"points": [v(9.5, 12.35) * mm, v(9.88, 11.55) * mm, v(9.9, 10.95) * mm], "startDerivative": vector(-2.6, -1.92) * mm, "endDerivative": vector(-1.81, -3.2) * mm});
            skFitSpline(sketch, "E140", {"points": [v(9.9, 10.95) * mm, v(10.84, 10.48) * mm, v(11.35, 10.95) * mm], "startDerivative": vector(-1.75, -3.5) * mm, "endDerivative": vector(3.25, 0.15) * mm});
            skFitSpline(sketch, "E141", {"points": [v(11.35, 10.95) * mm, v(11.35, 11.4) * mm, v(12.07, 11.7) * mm], "startDerivative": vector(4.92, 1.59) * mm, "endDerivative": vector(3.43, -0.74) * mm});
            skFitSpline(sketch, "E142", {"points": [v(12.07, 11.7) * mm, v(12.37, 12.3) * mm, v(12.9, 13.53) * mm], "startDerivative": vector(5.92, 3.23) * mm, "endDerivative": vector(7.21, 3.9) * mm});
            skFitSpline(sketch, "E143", {"points": [v(12.9, 13.53) * mm, v(12.64, 14.06) * mm, v(12.9, 15.03) * mm], "startDerivative": vector(3.19, 4.14) * mm, "endDerivative": vector(3.3, 3.05) * mm});
            skFitSpline(sketch, "E144", {"points": [v(12.9, 15.03) * mm, v(12.48, 15.62) * mm, v(12.46, 15.97) * mm], "startDerivative": vector(2.85, 4.1) * mm, "endDerivative": vector(1.72, 3.44) * mm});
            skFitSpline(sketch, "E145", {"points": [v(12.46, 15.97) * mm, v(11.93, 16.43) * mm, v(11.28, 16.25) * mm], "startDerivative": vector(-4.49, -1.55) * mm, "endDerivative": vector(-1.5, -4.15) * mm});
            skFitSpline(sketch, "E146.trimOffspring", {"points": [v(9.9, 10.95) * mm, v(10.84, 10.48) * mm, v(11.35, 10.95) * mm], "startDerivative": vector(-1.75, -3.5) * mm, "endDerivative": vector(3.25, 0.15) * mm});
            skFitSpline(sketch, "E147", {"points": [v(-20.75, 6.72) * mm, v(-21.02, 6.08) * mm, v(-20, 5.62) * mm], "startDerivative": vector(3.98, -2.7) * mm, "endDerivative": vector(-2.82, -2.72) * mm});
            skFitSpline(sketch, "E148", {"points": [v(-20, 5.62) * mm, v(-19.18, 5.26) * mm, v(-18.86, 4.68) * mm], "startDerivative": vector(-1.83, -4.95) * mm, "endDerivative": vector(-2.37, -4.2) * mm});
            skFitSpline(sketch, "E149", {"points": [v(-18.86, 4.68) * mm, v(-17.76, 4.74) * mm, v(-17.13, 4.45) * mm], "startDerivative": vector(-0.31, -4.22) * mm, "endDerivative": vector(-0.35, -4.99) * mm});
            skFitSpline(sketch, "E150", {"points": [v(-17.13, 4.45) * mm, v(-16.28, 4.7) * mm, v(-15.68, 4.65) * mm], "startDerivative": vector(1.56, -2.84) * mm, "endDerivative": vector(2.94, -2.22) * mm});
            skFitSpline(sketch, "E151", {"points": [v(-15.68, 4.65) * mm, v(-15.1, 5.52) * mm, v(-15.49, 6.09) * mm], "startDerivative": vector(3.24, -2.2) * mm, "endDerivative": vector(0.28, 3.24) * mm});
            skFitSpline(sketch, "E152", {"points": [v(-15.49, 6.09) * mm, v(-15.95, 6.15) * mm, v(-16.15, 6.9) * mm], "startDerivative": vector(-0.92, 5.1) * mm, "endDerivative": vector(1.18, 3.3) * mm});
            skFitSpline(sketch, "E153", {"points": [v(-16.15, 6.9) * mm, v(-16.7, 7.27) * mm, v(-17.84, 7.96) * mm], "startDerivative": vector(-2.41, 6.3) * mm, "endDerivative": vector(-2.9, 7.67) * mm});
            skFitSpline(sketch, "E154", {"points": [v(-17.84, 7.96) * mm, v(-18.4, 7.78) * mm, v(-19.33, 8.16) * mm], "startDerivative": vector(-3.68, 3.71) * mm, "endDerivative": vector(-2.59, 3.67) * mm});
            skFitSpline(sketch, "E155", {"points": [v(-19.33, 8.16) * mm, v(-19.97, 7.83) * mm, v(-20.32, 7.85) * mm], "startDerivative": vector(-3.68, 3.37) * mm, "endDerivative": vector(-3.18, 2.16) * mm});
            skFitSpline(sketch, "E156", {"points": [v(-20.32, 7.85) * mm, v(-20.85, 7.39) * mm, v(-20.75, 6.72) * mm], "startDerivative": vector(0.94, -4.65) * mm, "endDerivative": vector(3.92, -2.04) * mm});
            skFitSpline(sketch, "E157.trimOffspring", {"points": [v(-16.19, 5.22) * mm, v(-8.74, 4.58) * mm, v(-1.35, -0.04) * mm], "startDerivative": vector(17.65, -9.43) * mm, "endDerivative": vector(16.64, -25.54) * mm});
            skArc(sketch, "E158.filletArc", {"start": v(-15.53, 10.6) * mm, "mid": v(-14.99, 10.13) * mm, "end": v(-14.38, 9.75) * mm});
            skArc(sketch, "E159.filletArc", {"start": v(-14.73, 10.47) * mm, "mid": v(-14.77, 10.37) * mm, "end": v(-14.7, 10.28) * mm});
            skFitSpline(sketch, "E160", {"points": [v(-15.93, -11.44) * mm, v(-15.33, -11.79) * mm, v(-14.74, -10.82) * mm], "startDerivative": vector(3.2, 3.6) * mm, "endDerivative": vector(2.34, -3.14) * mm});
            skFitSpline(sketch, "E161", {"points": [v(-14.74, -10.82) * mm, v(-14.28, -10.07) * mm, v(-13.66, -9.83) * mm], "startDerivative": vector(4.67, -2.45) * mm, "endDerivative": vector(3.87, -2.9) * mm});
            skFitSpline(sketch, "E162", {"points": [v(-13.66, -9.83) * mm, v(-13.58, -8.73) * mm, v(-13.2, -8.13) * mm], "startDerivative": vector(4.14, -0.85) * mm, "endDerivative": vector(4.9, -1) * mm});
            skFitSpline(sketch, "E163", {"points": [v(-13.2, -8.13) * mm, v(-13.36, -7.26) * mm, v(-13.24, -6.59) * mm], "startDerivative": vector(3.01, 1.18) * mm, "endDerivative": vector(2.58, 2.63) * mm});
            skFitSpline(sketch, "E164", {"points": [v(-13.24, -6.59) * mm, v(-14.04, -5.9) * mm, v(-14.65, -6.2) * mm], "startDerivative": vector(2.6, 2.93) * mm, "endDerivative": vector(-3.18, 0.7) * mm});
            skFitSpline(sketch, "E165", {"points": [v(-14.65, -6.2) * mm, v(-14.77, -6.66) * mm, v(-15.51, -6.85) * mm], "startDerivative": vector(-5.17, -0.26) * mm, "endDerivative": vector(-3.12, 1.6) * mm});
            skFitSpline(sketch, "E166", {"points": [v(-15.51, -6.85) * mm, v(-15.96, -7.35) * mm, v(-16.79, -8.4) * mm], "startDerivative": vector(-6.55, -1.59) * mm, "endDerivative": vector(-7.98, -1.9) * mm});
            skFitSpline(sketch, "E167", {"points": [v(-16.79, -8.4) * mm, v(-16.68, -8.97) * mm, v(-17.17, -9.84) * mm], "startDerivative": vector(-4.15, -3.18) * mm, "endDerivative": vector(-3.98, -2.1) * mm});
            skFitSpline(sketch, "E168", {"points": [v(-17.17, -9.84) * mm, v(-16.93, -10.52) * mm, v(-17, -10.87) * mm], "startDerivative": vector(-3.81, -3.21) * mm, "endDerivative": vector(-2.55, -2.88) * mm});
            skFitSpline(sketch, "E169", {"points": [v(-17, -10.87) * mm, v(-16.6, -11.45) * mm, v(-15.93, -11.44) * mm], "startDerivative": vector(4.74, 0.34) * mm, "endDerivative": vector(2.52, 3.62) * mm});
            skLineSegment(sketch, "E170.0", {"start": v(-15.33, -11.79) * mm, "end": v(-16.6, -11.45) * mm, "construction": true});
            skLineSegment(sketch, "E171.0", {"start": v(-13.24, -6.59) * mm, "end": v(-14.65, -6.2) * mm, "construction": true});
            skLineSegment(sketch, "E172.0", {"start": v(-15.47, -10.9) * mm, "end": v(-16.93, -10.52) * mm, "construction": true});
            skLineSegment(sketch, "E173.0", {"start": v(-13.2, -8.13) * mm, "end": v(-13.66, -9.83) * mm, "construction": true});
            skLineSegment(sketch, "E174.0", {"start": v(-16.79, -8.4) * mm, "end": v(-17.17, -9.84) * mm, "construction": true});
            skLineSegment(sketch, "E175.0", {"start": v(-14.65, -6.2) * mm, "end": v(-14.77, -6.66) * mm, "construction": true});
            skFitSpline(sketch, "E176.trimOffspring", {"points": [v(-18.96, -5.83) * mm, v(-1.16, -18.25) * mm, v(-8.26, -37.47) * mm], "startDerivative": vector(95.98, 3.77) * mm, "endDerivative": vector(-30.97, -39) * mm});
            skPoint(sketch, "E177.visualSharp", {"position": v(-13.58, -5.9) * mm});
            skArc(sketch, "E177.filletArc", {"start": v(-13.09, -5.95) * mm, "mid": v(-13.2, -6) * mm, "end": v(-13.18, -6.12) * mm});
            skFitSpline(sketch, "E178", {"points": [v(13.12, 5.05) * mm, v(12.87, 4.5) * mm, v(12.74, 4.24) * mm], "startDerivative": vector(-3.94, -1.68) * mm, "endDerivative": vector(-2.93, -0.2) * mm});
            skFitSpline(sketch, "E179", {"points": [v(13.12, 5.05) * mm, v(13.73, 5.06) * mm, v(14.07, 4.89) * mm], "startDerivative": vector(0.85, 3.96) * mm, "endDerivative": vector(2.32, 1.4) * mm});
            skFitSpline(sketch, "E180", {"points": [v(12.74, 4.24) * mm, v(12.94, 3.82) * mm, v(12.93, 3.47) * mm], "startDerivative": vector(-2.64, -0.64) * mm, "endDerivative": vector(-1.9, -1.25) * mm});
            skFitSpline(sketch, "E181", {"points": [v(12.93, 3.47) * mm, v(13.29, 3.15) * mm, v(13.55, 2.95) * mm], "startDerivative": vector(-1.26, -1.07) * mm, "endDerivative": vector(-0.2, -2.18) * mm});
            skFitSpline(sketch, "E182", {"points": [v(14.07, 4.89) * mm, v(14.07, 4.43) * mm, v(14.43, 4.34) * mm], "startDerivative": vector(3.22, 0.96) * mm, "endDerivative": vector(0.96, -0.02) * mm});
            skFitSpline(sketch, "E183", {"points": [v(14.43, 4.34) * mm, v(14.31, 3.9) * mm, v(14.28, 3.6) * mm], "startDerivative": vector(2.09, -0.19) * mm, "endDerivative": vector(3.54, -0.82) * mm});
            skFitSpline(sketch, "E184", {"points": [v(14.28, 3.6) * mm, v(14.22, 3.2) * mm, v(13.55, 2.95) * mm], "startDerivative": vector(-3.92, -2.3) * mm, "endDerivative": vector(-1.83, 3.45) * mm});
            skFitSpline(sketch, "E185", {"points": [v(17.96, 3.35) * mm, v(17.4, 3.17) * mm, v(17.11, 3.1) * mm], "startDerivative": vector(-3.9, 1.77) * mm, "endDerivative": vector(-2.13, 2.03) * mm});
            skFitSpline(sketch, "E186", {"points": [v(17.96, 3.35) * mm, v(18.38, 2.91) * mm, v(18.49, 2.54) * mm], "startDerivative": vector(3.5, 2.04) * mm, "endDerivative": vector(2.6, -0.78) * mm});
            skFitSpline(sketch, "E187", {"points": [v(17.11, 3.1) * mm, v(16.93, 2.66) * mm, v(16.66, 2.43) * mm], "startDerivative": vector(-2.26, 1.52) * mm, "endDerivative": vector(-2.2, 0.56) * mm});
            skFitSpline(sketch, "E188", {"points": [v(16.66, 2.43) * mm, v(16.67, 1.95) * mm, v(16.65, 1.51) * mm], "startDerivative": vector(-1.64, 0.21) * mm, "endDerivative": vector(-1.75, -1.32) * mm});
            skFitSpline(sketch, "E189", {"points": [v(18.49, 2.54) * mm, v(18.14, 2.24) * mm, v(18.33, 1.9) * mm], "startDerivative": vector(2.87, -1.73) * mm, "endDerivative": vector(0.63, -0.72) * mm});
            skFitSpline(sketch, "E190", {"points": [v(18.33, 1.9) * mm, v(17.92, 1.7) * mm, v(17.67, 1.52) * mm], "startDerivative": vector(1.27, -1.67) * mm, "endDerivative": vector(1.78, -3.17) * mm});
            skFitSpline(sketch, "E191", {"points": [v(17.67, 1.52) * mm, v(17.33, 1.3) * mm, v(16.65, 1.51) * mm], "startDerivative": vector(-4.35, 1.34) * mm, "endDerivative": vector(1.32, 3.68) * mm});
            skArc(sketch, "E192.filletArc", {"start": v(17.45, 1.58) * mm, "mid": v(17.55, 1.6) * mm, "end": v(17.57, 1.72) * mm});
            skArc(sketch, "E193.filletArc", {"start": v(14.1, 3.47) * mm, "mid": v(14.13, 3.57) * mm, "end": v(14.07, 3.66) * mm});
            skFitSpline(sketch, "E194", {"points": [v(14.68, -1.28) * mm, v(15.18, -0.96) * mm, v(15.44, -0.8) * mm], "startDerivative": vector(4.22, -0.7) * mm, "endDerivative": vector(2.58, -1.4) * mm});
            skFitSpline(sketch, "E195", {"points": [v(14.68, -1.28) * mm, v(14.16, -0.97) * mm, v(13.97, -0.63) * mm], "startDerivative": vector(-2.85, -2.88) * mm, "endDerivative": vector(-2.7, 0.08) * mm});
            skFitSpline(sketch, "E196", {"points": [v(15.44, -0.8) * mm, v(15.5, -0.35) * mm, v(15.7, -0.05) * mm], "startDerivative": vector(2.57, -0.88) * mm, "endDerivative": vector(2.27, 0.03) * mm});
            skFitSpline(sketch, "E197", {"points": [v(15.7, -0.05) * mm, v(15.57, 0.4) * mm, v(15.47, 0.86) * mm], "startDerivative": vector(1.64, 0.22) * mm, "endDerivative": vector(1.35, 1.73) * mm});
            skFitSpline(sketch, "E198", {"points": [v(13.97, -0.63) * mm, v(14.22, -0.25) * mm, v(13.96, 0.02) * mm], "startDerivative": vector(-3.22, 0.93) * mm, "endDerivative": vector(-0.8, 0.53) * mm});
            skFitSpline(sketch, "E199", {"points": [v(13.96, 0.02) * mm, v(14.3, 0.32) * mm, v(14.5, 0.57) * mm], "startDerivative": vector(-1.66, 1.28) * mm, "endDerivative": vector(-2.54, 2.6) * mm});
            skFitSpline(sketch, "E200", {"points": [v(14.5, 0.57) * mm, v(14.76, 0.87) * mm, v(15.47, 0.86) * mm], "startDerivative": vector(4.55, -0.17) * mm, "endDerivative": vector(-0.32, -3.9) * mm});
            skFitSpline(sketch, "E201", {"points": [v(-20.78, 0.66) * mm, v(-20.27, 0.36) * mm, v(-20.02, 0.2) * mm], "startDerivative": vector(1.3, -4.08) * mm, "endDerivative": vector(-0.08, -2.94) * mm});
            skFitSpline(sketch, "E202", {"points": [v(-20.78, 0.66) * mm, v(-20.74, 1.26) * mm, v(-20.53, 1.6) * mm], "startDerivative": vector(-3.86, 1.23) * mm, "endDerivative": vector(-1.16, 2.45) * mm});
            skFitSpline(sketch, "E203", {"points": [v(-20.02, 0.2) * mm, v(-19.58, 0.36) * mm, v(-19.23, 0.3) * mm], "startDerivative": vector(0.38, -2.7) * mm, "endDerivative": vector(1.06, -2.01) * mm});
            skFitSpline(sketch, "E204", {"points": [v(-19.23, 0.3) * mm, v(-18.88, 0.64) * mm, v(-18.5, 0.94) * mm], "startDerivative": vector(0.94, -1.36) * mm, "endDerivative": vector(2.15, -0.42) * mm});
            skFitSpline(sketch, "E205", {"points": [v(-20.53, 1.6) * mm, v(-20.08, 1.54) * mm, v(-19.95, 1.9) * mm], "startDerivative": vector(-0.64, 3.3) * mm, "endDerivative": vector(0.11, 0.95) * mm});
            skFitSpline(sketch, "E206", {"points": [v(-19.95, 1.9) * mm, v(-19.53, 1.73) * mm, v(-19.22, 1.67) * mm], "startDerivative": vector(0.4, 2.06) * mm, "endDerivative": vector(1.16, 3.44) * mm});
            skFitSpline(sketch, "E207", {"points": [v(-19.22, 1.67) * mm, v(-18.83, 1.57) * mm, v(-18.5, 0.94) * mm], "startDerivative": vector(1.91, -4.13) * mm, "endDerivative": vector(-3.61, -1.48) * mm});
            skFitSpline(sketch, "E208", {"points": [v(-19.54, -5.33) * mm, v(-19.22, -5.83) * mm, v(-19.07, -6.1) * mm], "startDerivative": vector(-0.7, -4.22) * mm, "endDerivative": vector(-1.4, -2.58) * mm});
            skFitSpline(sketch, "E209", {"points": [v(-19.54, -5.33) * mm, v(-19.23, -4.81) * mm, v(-18.9, -4.62) * mm], "startDerivative": vector(-2.88, 2.85) * mm, "endDerivative": vector(0.08, 2.7) * mm});
            skFitSpline(sketch, "E210", {"points": [v(-19.07, -6.1) * mm, v(-18.61, -6.15) * mm, v(-18.32, -6.35) * mm], "startDerivative": vector(-0.88, -2.57) * mm, "endDerivative": vector(0.03, -2.27) * mm});
            skFitSpline(sketch, "E211", {"points": [v(-18.32, -6.35) * mm, v(-17.85, -6.22) * mm, v(-17.4, -5.79) * mm], "startDerivative": vector(0.22, -1.64) * mm, "endDerivative": vector(1.73, -1.35) * mm});
            skFitSpline(sketch, "E212", {"points": [v(-18.9, -4.62) * mm, v(-18.52, -4.87) * mm, v(-18.24, -4.61) * mm], "startDerivative": vector(0.93, 3.22) * mm, "endDerivative": vector(0.53, 0.8) * mm});
            skFitSpline(sketch, "E213", {"points": [v(-18.24, -4.61) * mm, v(-17.94, -4.94) * mm, v(-17.67, -5.14) * mm], "startDerivative": vector(1.28, 1.66) * mm, "endDerivative": vector(2.6, 2.54) * mm});
            skFitSpline(sketch, "E214", {"points": [v(-17.67, -5.14) * mm, v(-17.37, -5.36) * mm, v(-17.4, -5.79) * mm], "startDerivative": vector(-0.17, -4.55) * mm, "endDerivative": vector(-3.9, 0.32) * mm});
            skFitSpline(sketch, "E215", {"points": [v(5.05, 22.13) * mm, v(4.46, 22.2) * mm, v(4.17, 22.26) * mm], "startDerivative": vector(-2.78, 3.25) * mm, "endDerivative": vector(-1.07, 2.74) * mm});
            skFitSpline(sketch, "E216", {"points": [v(5.05, 22.13) * mm, v(5.25, 21.56) * mm, v(5.18, 21.18) * mm], "startDerivative": vector(4.04, 0.37) * mm, "endDerivative": vector(2.03, -1.8) * mm});
            skFitSpline(sketch, "E217", {"points": [v(4.17, 22.26) * mm, v(3.83, 21.94) * mm, v(3.48, 21.85) * mm], "startDerivative": vector(-1.4, 2.33) * mm, "endDerivative": vector(-1.76, 1.44) * mm});
            skFitSpline(sketch, "E218", {"points": [v(3.48, 21.85) * mm, v(3.28, 21.4) * mm, v(3.14, 21.02) * mm], "startDerivative": vector(-1.4, 0.88) * mm, "endDerivative": vector(-2.15, -0.46) * mm});
            skFitSpline(sketch, "E219", {"points": [v(5.18, 21.18) * mm, v(4.74, 21.05) * mm, v(4.77, 20.67) * mm], "startDerivative": vector(1.87, -2.78) * mm, "endDerivative": vector(0.27, -0.92) * mm});
            skFitSpline(sketch, "E220", {"points": [v(4.77, 20.67) * mm, v(4.32, 20.66) * mm, v(4.01, 20.6) * mm], "startDerivative": vector(0.44, -2.05) * mm, "endDerivative": vector(0.28, -3.62) * mm});
            skFitSpline(sketch, "E221", {"points": [v(4.01, 20.6) * mm, v(3.6, 20.53) * mm, v(3.14, 21.02) * mm], "startDerivative": vector(-3.37, 3.06) * mm, "endDerivative": vector(2.75, 2.78) * mm});
            skFitSpline(sketch, "E222", {"points": [v(-6.82, 10.34) * mm, v(-7.17, 9.75) * mm, v(-6.2, 9.15) * mm], "startDerivative": vector(3.6, -3.2) * mm, "endDerivative": vector(-3.14, -2.34) * mm});
            skFitSpline(sketch, "E223", {"points": [v(-6.2, 9.15) * mm, v(-5.45, 8.69) * mm, v(-5.2, 8.07) * mm], "startDerivative": vector(-2.45, -4.67) * mm, "endDerivative": vector(-2.9, -3.87) * mm});
            skFitSpline(sketch, "E224", {"points": [v(-5.2, 8.07) * mm, v(-4.1, 8) * mm, v(-3.51, 7.62) * mm], "startDerivative": vector(-0.85, -4.14) * mm, "endDerivative": vector(-1, -4.9) * mm});
            skFitSpline(sketch, "E225", {"points": [v(-3.51, 7.62) * mm, v(-2.64, 7.77) * mm, v(-2.05, 7.63) * mm], "startDerivative": vector(1.18, -3.01) * mm, "endDerivative": vector(2.63, -2.58) * mm});
            skFitSpline(sketch, "E226", {"points": [v(-2.05, 7.63) * mm, v(-1.36, 8.43) * mm, v(-1.68, 9.04) * mm], "startDerivative": vector(2.93, -2.6) * mm, "endDerivative": vector(0.7, 3.18) * mm});
            skFitSpline(sketch, "E227", {"points": [v(-1.68, 9.04) * mm, v(-2.12, 9.16) * mm, v(-2.23, 9.92) * mm], "startDerivative": vector(-0.26, 5.17) * mm, "endDerivative": vector(1.6, 3.12) * mm});
            skFitSpline(sketch, "E228", {"points": [v(-2.23, 9.92) * mm, v(-2.73, 10.37) * mm, v(-3.77, 11.2) * mm], "startDerivative": vector(-1.59, 6.55) * mm, "endDerivative": vector(-1.9, 7.98) * mm});
            skFitSpline(sketch, "E229", {"points": [v(-3.77, 11.2) * mm, v(-4.35, 11.1) * mm, v(-5.22, 11.59) * mm], "startDerivative": vector(-3.18, 4.15) * mm, "endDerivative": vector(-2.1, 3.98) * mm});
            skFitSpline(sketch, "E230", {"points": [v(-5.22, 11.59) * mm, v(-5.9, 11.34) * mm, v(-6.25, 11.4) * mm], "startDerivative": vector(-3.21, 3.81) * mm, "endDerivative": vector(-2.88, 2.55) * mm});
            skFitSpline(sketch, "E231", {"points": [v(-6.25, 11.4) * mm, v(-6.83, 11.01) * mm, v(-6.82, 10.34) * mm], "startDerivative": vector(0.34, -4.74) * mm, "endDerivative": vector(3.62, -2.52) * mm});
            skFitSpline(sketch, "E232.trimOffspring", {"points": [v(-2.05, 7.63) * mm, v(-1.36, 8.43) * mm, v(-1.68, 9.04) * mm], "startDerivative": vector(2.93, -2.6) * mm, "endDerivative": vector(0.7, 3.18) * mm});
            skLineSegment(sketch, "E233.0", {"start": v(-7.17, 9.75) * mm, "end": v(-6.83, 11.01) * mm, "construction": true});
            skLineSegment(sketch, "E234.0", {"start": v(-2.05, 7.63) * mm, "end": v(-1.68, 9.04) * mm, "construction": true});
            skLineSegment(sketch, "E235.0", {"start": v(-6.3, 9.88) * mm, "end": v(-5.9, 11.34) * mm, "construction": true});
            skLineSegment(sketch, "E236.0", {"start": v(-3.77, 11.2) * mm, "end": v(-5.22, 11.59) * mm, "construction": true});
            skLineSegment(sketch, "E237.0", {"start": v(-3.51, 7.62) * mm, "end": v(-5.2, 8.07) * mm, "construction": true});
            skLineSegment(sketch, "E238.0", {"start": v(-1.68, 9.04) * mm, "end": v(-2.12, 9.16) * mm, "construction": true});
            skPoint(sketch, "E239.visualSharp", {"position": v(-1.4, 7.86) * mm});
            skArc(sketch, "E239.filletArc", {"start": v(-1.37, 7.54) * mm, "mid": v(-1.44, 7.63) * mm, "end": v(-1.55, 7.6) * mm});
            skFitSpline(sketch, "E240", {"points": [v(4.1, 8.4) * mm, v(3.53, 8.73) * mm, v(2.8, 8.05) * mm], "startDerivative": vector(-3.87, -2.86) * mm, "endDerivative": vector(-1.63, 3.56) * mm});
            skFitSpline(sketch, "E241", {"points": [v(2.8, 8.05) * mm, v(2.2, 7.4) * mm, v(1.76, 7.19) * mm], "startDerivative": vector(-4.06, 3.37) * mm, "endDerivative": vector(-3.18, 3.63) * mm});
            skFitSpline(sketch, "E242", {"points": [v(1.76, 7.19) * mm, v(1.24, 6.24) * mm, v(1.23, 5.73) * mm], "startDerivative": vector(-3.88, 1.7) * mm, "endDerivative": vector(-4.59, 1.99) * mm});
            skFitSpline(sketch, "E243", {"points": [v(1.23, 5.73) * mm, v(0.7, 4.85) * mm, v(0.36, 4.19) * mm], "startDerivative": vector(-1.13, 4.75) * mm, "endDerivative": vector(-3.07, -2.04) * mm});
            skFitSpline(sketch, "E244", {"points": [v(1.72, 3.68) * mm, v(1.87, 4.1) * mm, v(2.73, 4) * mm], "startDerivative": vector(5, -3.58) * mm, "endDerivative": vector(2.72, -2.21) * mm});
            skFitSpline(sketch, "E245", {"points": [v(2.73, 4) * mm, v(3.27, 4.4) * mm, v(4.47, 5.19) * mm], "startDerivative": vector(6.74, 0.19) * mm, "endDerivative": vector(8.2, 0.2) * mm});
            skFitSpline(sketch, "E246", {"points": [v(4.47, 5.19) * mm, v(4.32, 5.83) * mm, v(4.98, 6.58) * mm], "startDerivative": vector(4.72, 2.25) * mm, "endDerivative": vector(4.33, 1.22) * mm});
            skFitSpline(sketch, "E247", {"points": [v(4.98, 6.58) * mm, v(4.94, 7.45) * mm, v(5.02, 7.62) * mm], "startDerivative": vector(4.4, 2.35) * mm, "endDerivative": vector(3.1, 2.28) * mm});
            skFitSpline(sketch, "E248", {"points": [v(5.02, 7.62) * mm, v(4.76, 8.27) * mm, v(4.1, 8.4) * mm], "startDerivative": vector(-4.7, 0.65) * mm, "endDerivative": vector(-3.22, -3.02) * mm});
            skFitSpline(sketch, "E249.trimOffspring", {"points": [v(0.36, 4.19) * mm, v(1, 3.11) * mm, v(1.72, 3.68) * mm], "startDerivative": vector(-1.8, -3.5) * mm, "endDerivative": vector(1.06, -3.08) * mm});
            skLineSegment(sketch, "E250.0", {"start": v(3.53, 8.73) * mm, "end": v(4.76, 8.27) * mm, "construction": true});
            skLineSegment(sketch, "E251.0", {"start": v(3.52, 7.98) * mm, "end": v(4.94, 7.45) * mm, "construction": true});
            skLineSegment(sketch, "E252.0", {"start": v(4.47, 5.19) * mm, "end": v(4.98, 6.58) * mm, "construction": true});
            skLineSegment(sketch, "E253.0", {"start": v(1.23, 5.73) * mm, "end": v(1.76, 7.19) * mm, "construction": true});
            skFitSpline(sketch, "E254", {"points": [v(11.77, -5.01) * mm, v(12.2, -4.48) * mm, v(11.37, -3.73) * mm], "startDerivative": vector(-3, 3.77) * mm, "endDerivative": vector(3.5, 1.76) * mm});
            skFitSpline(sketch, "E255", {"points": [v(11.37, -3.73) * mm, v(10.7, -3.14) * mm, v(10.57, -2.5) * mm], "startDerivative": vector(3.23, 4.18) * mm, "endDerivative": vector(3.52, 3.3) * mm});
            skFitSpline(sketch, "E256", {"points": [v(10.57, -2.5) * mm, v(9.5, -2.23) * mm, v(8.98, -1.78) * mm], "startDerivative": vector(1.56, 3.93) * mm, "endDerivative": vector(1.83, 4.66) * mm});
            skFitSpline(sketch, "E257", {"points": [v(8.98, -1.78) * mm, v(8.1, -1.75) * mm, v(7.54, -1.5) * mm], "startDerivative": vector(-0.64, 3.17) * mm, "endDerivative": vector(-2.14, 3) * mm});
            skFitSpline(sketch, "E258", {"points": [v(7.54, -1.5) * mm, v(6.46, -2.15) * mm, v(6.95, -2.81) * mm], "startDerivative": vector(-3.13, 2.35) * mm, "endDerivative": vector(-2, -2.56) * mm});
            skFitSpline(sketch, "E259", {"points": [v(6.95, -2.81) * mm, v(7.36, -3) * mm, v(7.32, -3.8) * mm], "startDerivative": vector(-0.64, -5.13) * mm, "endDerivative": vector(-2.12, -2.8) * mm});
            skFitSpline(sketch, "E260", {"points": [v(7.32, -3.8) * mm, v(7.74, -4.33) * mm, v(8.61, -5.35) * mm], "startDerivative": vector(0.42, -6.73) * mm, "endDerivative": vector(0.49, -8.18) * mm});
            skFitSpline(sketch, "E261", {"points": [v(8.61, -5.35) * mm, v(9.2, -5.32) * mm, v(9.98, -5.96) * mm], "startDerivative": vector(2.4, -4.64) * mm, "endDerivative": vector(1.37, -4.28) * mm});
            skFitSpline(sketch, "E262", {"points": [v(9.98, -5.96) * mm, v(10.7, -5.84) * mm, v(11.02, -5.96) * mm], "startDerivative": vector(2.5, -4.31) * mm, "endDerivative": vector(2.4, -3.01) * mm});
            skFitSpline(sketch, "E263", {"points": [v(11.02, -5.96) * mm, v(11.66, -5.68) * mm, v(11.77, -5.01) * mm], "startDerivative": vector(0.49, 4.72) * mm, "endDerivative": vector(-3.13, 3.12) * mm});
            skLineSegment(sketch, "E264.0", {"start": v(12.2, -4.48) * mm, "end": v(11.66, -5.68) * mm, "construction": true});
            skFitSpline(sketch, "E265.trimOffspring", {"points": [v(11.85, 1.07) * mm, v(2.54, -18.35) * mm, v(5.68, -37.82) * mm], "startDerivative": vector(-64.96, -24.6) * mm, "endDerivative": vector(16.53, -39.43) * mm});
            skFitSpline(sketch, "E266", {"points": [v(-12.46, 3.4) * mm, v(-12.83, 2.5) * mm, v(-13.16, 2.2) * mm], "startDerivative": vector(-5.31, 1.96) * mm, "endDerivative": vector(-2.93, 0.23) * mm});
            skFitSpline(sketch, "E267", {"points": [v(-12.46, 3.4) * mm, v(-11.4, 3.46) * mm, v(-11.1, 3.11) * mm], "startDerivative": vector(3.12, 4.97) * mm, "endDerivative": vector(2.5, 1.03) * mm});
            skFitSpline(sketch, "E268", {"points": [v(-13.16, 2.2) * mm, v(-12.96, 1.41) * mm, v(-13.02, 1.06) * mm], "startDerivative": vector(-2.7, -0.24) * mm, "endDerivative": vector(-2.06, -0.95) * mm});
            skFitSpline(sketch, "E269", {"points": [v(-13.02, 1.06) * mm, v(-12.8, 0.7) * mm, v(-12.76, 0.42) * mm], "startDerivative": vector(-1.4, -0.87) * mm, "endDerivative": vector(-0.53, -2.13) * mm});
            skFitSpline(sketch, "E270", {"points": [v(-11.1, 3.11) * mm, v(-11.27, 2.34) * mm, v(-11.05, 2.06) * mm], "startDerivative": vector(3.32, 0.47) * mm, "endDerivative": vector(0.94, -0.16) * mm});
            skFitSpline(sketch, "E271", {"points": [v(-11.05, 2.06) * mm, v(-11.4, 1.49) * mm, v(-11.82, 0.6) * mm], "startDerivative": vector(2.04, -0.5) * mm, "endDerivative": vector(-7.33, -2.3) * mm});
            skFitSpline(sketch, "E272", {"points": [v(-11.82, 0.6) * mm, v(-12.02, 0.1) * mm, v(-12.76, 0.42) * mm], "startDerivative": vector(-1.9, -4.2) * mm, "endDerivative": vector(-3.7, 1.25) * mm});
            skArc(sketch, "E273.filletArc", {"start": v(-11.77, 0.62) * mm, "mid": v(-11.81, 0.6) * mm, "end": v(-11.84, 0.57) * mm});
            skSolve(sketch);
        }
        {
            var Q0;
            Q0=makeQuery(id+"F0.imprint","IMPRINT",FACE,{"disambiguationData":[TD([[makeQuery(id+"F0.imprint","IMPRINT",EDGE,{"derivedFrom":sQuery(id+"F0.wireOp",EDGE,"E0")}),1.0]])]});
            var Q1;
            {var subQ0=sQuery(id+"F0.wireOp",EDGE,"E38");var subQ1=sQuery(id+"F0.wireOp",EDGE,"E3");var subQ2=makeQuery(id+"F0.imprint","INTERSECT",VERTEX,{"derivedFrom":[subQ1,subQ0]});Q1=makeQuery(id+"F0.imprint","IMPRINT",FACE,{"disambiguationData":[TD([[makeQuery(id+"F0.imprint","IMPRINT",EDGE,{"disambiguationData":[TD([[subQ2,-1.0]])],"derivedFrom":subQ1}),1.0]])]});}
            extrude(context, id + "F1", {"entities" : qUnion([Q0, Q1]), "depth" : 2 * mm, "offsetDistance" : 25 * mm});
        }
    });
